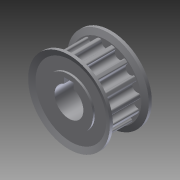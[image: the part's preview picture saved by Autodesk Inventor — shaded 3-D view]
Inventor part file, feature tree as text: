
AUTODESK INVENTOR PART (.ipt)
format: ipt  version: 2012 (Build 160160000, 160)  size: 306,176 bytes
history: native  units: in
note: dims shown in document units (in); Inventor stores cm internally (conversion verified against a paired STEP export)
features: extrude x2, sketch x2, imported_body x1
ambient origin geometry x8: Origin, YZ Plane, XZ Plane, XY Plane, X Axis, Y Axis, Z Axis, Center Point
feature tree (5):
  extrude  "Extrusion1"  Depth=0.0394in
  extrude  "Extrusion2"  Depth=0.125in
  imported_body  "Base1"
  sketch  "Sketch1"  dims[d0=0.375in d1=0.0394in d4=0.0625in]
  sketch  "Sketch2"  dims[d5=0.125in d6=0.125in d7=0.125in d8=0.3937in d9=0.0in d10=0.248in d11=0.0in]
